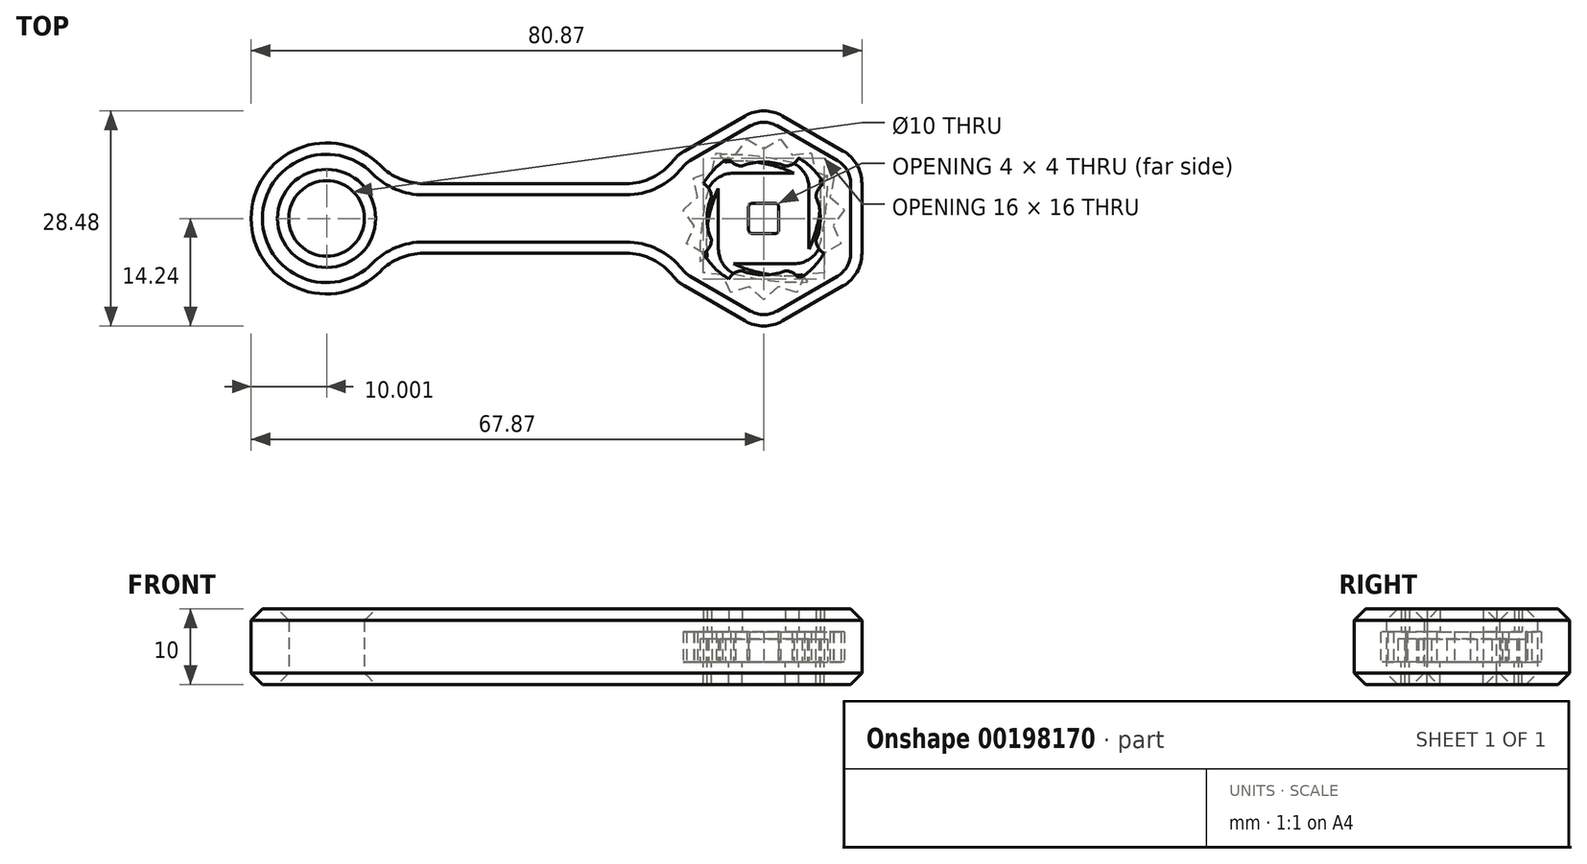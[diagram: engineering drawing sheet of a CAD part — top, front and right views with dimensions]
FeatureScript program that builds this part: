
annotation { "Feature Type Name" : "Feature", "Feature Type Description" : "" }
export const myFeature = defineFeature(function(context is Context, id is Id, definition is map)
    precondition{}
    {
        {
            var Q0;
            Q0=qCreatedBy(makeId("Top.planeOp"),FACE);
            var sketch = newSketch(context, id + "F0", { "sketchPlane" : qUnion([Q0])});
            skCircle(sketch, "E0.cCircle", {"center": v(0, 0) * mm, "radius": 13 * mm, "construction": true});
            skLineSegment(sketch, "E0.0", {"start": v(13, 4.62) * mm, "end": v(13, -4.62) * mm});
            skLineSegment(sketch, "E0.1", {"start": v(10.5, -8.95) * mm, "end": v(2.5, -13.57) * mm});
            skLineSegment(sketch, "E0.2", {"start": v(-2.5, -13.57) * mm, "end": v(-10.5, -8.95) * mm});
            skLineSegment(sketch, "E0.3", {"start": v(-13, -4.62) * mm, "end": v(-13, 4.62) * mm});
            skLineSegment(sketch, "E0.4", {"start": v(-10.5, 8.95) * mm, "end": v(-2.5, 13.57) * mm});
            skLineSegment(sketch, "E0.5", {"start": v(2.5, 13.57) * mm, "end": v(10.5, 8.95) * mm});
            skPoint(sketch, "E0.0.midPoint", {"position": v(13, 0) * mm});
            skPoint(sketch, "E1.visualSharp", {"position": v(0, 15.01) * mm});
            skArc(sketch, "E1.filletArc", {"start": v(2.5, 13.57) * mm, "mid": v(0, 14.24) * mm, "end": v(-2.5, 13.57) * mm});
            skPoint(sketch, "E2.visualSharp", {"position": v(13, 7.5) * mm});
            skArc(sketch, "E2.filletArc", {"start": v(13, 4.62) * mm, "mid": v(12.33, 7.12) * mm, "end": v(10.5, 8.95) * mm});
            skPoint(sketch, "E3.visualSharp", {"position": v(13, -7.5) * mm});
            skArc(sketch, "E3.filletArc", {"start": v(10.5, -8.95) * mm, "mid": v(12.33, -7.12) * mm, "end": v(13, -4.62) * mm});
            skPoint(sketch, "E4.visualSharp", {"position": v(0, -15.01) * mm});
            skArc(sketch, "E4.filletArc", {"start": v(-2.5, -13.57) * mm, "mid": v(0, -14.24) * mm, "end": v(2.5, -13.57) * mm});
            skPoint(sketch, "E5.visualSharp", {"position": v(-13, -7.5) * mm});
            skArc(sketch, "E5.filletArc", {"start": v(-13, -4.62) * mm, "mid": v(-12.33, -7.12) * mm, "end": v(-10.5, -8.95) * mm});
            skPoint(sketch, "E6.visualSharp", {"position": v(-13, 7.5) * mm});
            skArc(sketch, "E6.filletArc", {"start": v(-10.5, 8.95) * mm, "mid": v(-12.33, 7.12) * mm, "end": v(-13, 4.62) * mm});
            skCircle(sketch, "E7", {"center": v(0, 0) * mm, "radius": 9.24 * mm});
            skLineSegment(sketch, "E8", {"start": v(0, 9.24) * mm, "end": v(2.23, 10.5) * mm});
            skLineSegment(sketch, "E9", {"start": v(2.23, 10.5) * mm, "end": v(3.76, 8.44) * mm});
            skLineSegment(sketch, "E10.1.0", {"start": v(-3.76, 8.44) * mm, "end": v(-2.23, 10.5) * mm});
            skLineSegment(sketch, "E10.1.1", {"start": v(-2.23, 10.5) * mm, "end": v(0, 9.24) * mm});
            skLineSegment(sketch, "E10.2.0", {"start": v(-6.86, 6.18) * mm, "end": v(-6.31, 8.69) * mm});
            skLineSegment(sketch, "E10.2.1", {"start": v(-6.31, 8.69) * mm, "end": v(-3.76, 8.44) * mm});
            skLineSegment(sketch, "E10.3.0", {"start": v(-8.79, 2.85) * mm, "end": v(-9.3, 5.37) * mm});
            skLineSegment(sketch, "E10.3.1", {"start": v(-9.3, 5.37) * mm, "end": v(-6.86, 6.18) * mm});
            skLineSegment(sketch, "E10.4.0", {"start": v(-9.19, -0.97) * mm, "end": v(-10.68, 1.12) * mm});
            skLineSegment(sketch, "E10.4.1", {"start": v(-10.68, 1.12) * mm, "end": v(-8.79, 2.85) * mm});
            skLineSegment(sketch, "E10.5.0", {"start": v(-8, -4.62) * mm, "end": v(-10.21, -3.32) * mm});
            skLineSegment(sketch, "E10.5.1", {"start": v(-10.21, -3.32) * mm, "end": v(-9.19, -0.97) * mm});
            skLineSegment(sketch, "E10.6.0", {"start": v(-5.43, -7.47) * mm, "end": v(-7.98, -7.18) * mm});
            skLineSegment(sketch, "E10.6.1", {"start": v(-7.98, -7.18) * mm, "end": v(-8, -4.62) * mm});
            skLineSegment(sketch, "E10.7.0", {"start": v(-1.92, -9.04) * mm, "end": v(-4.37, -9.8) * mm});
            skLineSegment(sketch, "E10.7.1", {"start": v(-4.37, -9.8) * mm, "end": v(-5.43, -7.47) * mm});
            skLineSegment(sketch, "E10.8.0", {"start": v(1.92, -9.04) * mm, "end": v(0, -10.74) * mm});
            skLineSegment(sketch, "E10.8.1", {"start": v(0, -10.74) * mm, "end": v(-1.92, -9.04) * mm});
            skLineSegment(sketch, "E10.9.0", {"start": v(5.43, -7.47) * mm, "end": v(4.37, -9.8) * mm});
            skLineSegment(sketch, "E10.9.1", {"start": v(4.37, -9.8) * mm, "end": v(1.92, -9.04) * mm});
            skLineSegment(sketch, "E10.10.0", {"start": v(8, -4.62) * mm, "end": v(7.98, -7.18) * mm});
            skLineSegment(sketch, "E10.10.1", {"start": v(7.98, -7.18) * mm, "end": v(5.43, -7.47) * mm});
            skLineSegment(sketch, "E10.11.0", {"start": v(9.19, -0.97) * mm, "end": v(10.21, -3.32) * mm});
            skLineSegment(sketch, "E10.11.1", {"start": v(10.21, -3.32) * mm, "end": v(8, -4.62) * mm});
            skLineSegment(sketch, "E10.12.0", {"start": v(8.79, 2.85) * mm, "end": v(10.68, 1.12) * mm});
            skLineSegment(sketch, "E10.12.1", {"start": v(10.68, 1.12) * mm, "end": v(9.19, -0.97) * mm});
            skLineSegment(sketch, "E10.13.0", {"start": v(6.86, 6.18) * mm, "end": v(9.3, 5.37) * mm});
            skLineSegment(sketch, "E10.13.1", {"start": v(9.3, 5.37) * mm, "end": v(8.79, 2.85) * mm});
            skLineSegment(sketch, "E10.14.0", {"start": v(3.76, 8.44) * mm, "end": v(6.31, 8.69) * mm});
            skLineSegment(sketch, "E10.14.1", {"start": v(6.31, 8.69) * mm, "end": v(6.86, 6.18) * mm});
            skLineSegment(sketch, "E11.bottom", {"start": v(-13, 4.62) * mm, "end": v(-49, 4.62) * mm});
            skLineSegment(sketch, "E11.top", {"start": v(-13, -4.62) * mm, "end": v(-49, -4.62) * mm});
            skLineSegment(sketch, "E11.left", {"start": v(-13, 4.62) * mm, "end": v(-13, -4.62) * mm});
            skCircle(sketch, "E12", {"center": v(-57.87, 0) * mm, "radius": 5 * mm});
            skCircle(sketch, "E13", {"center": v(-57.87, 0) * mm, "radius": 10 * mm});
            skSolve(sketch);
        }
        {
            var Q0;
            Q0=makeQuery(id+"F0.imprint","IMPRINT",FACE,{"disambiguationData":[TD([[makeQuery(id+"F0.imprint","IMPRINT",EDGE,{"derivedFrom":sQuery(id+"F0.wireOp",EDGE,"E0.0")}),-1.0]])]});
            extrude(context, id + "F1", {"entities" : qUnion([Q0]), "endBound" : BoundingType.SYMMETRIC, "depth" : 4 * mm});
        }
        {
            var Q0;
            Q0=makeQuery(id+"F0.imprint","IMPRINT",FACE,{"disambiguationData":[TD([[makeQuery(id+"F0.imprint","IMPRINT",EDGE,{"derivedFrom":sQuery(id+"F0.wireOp",EDGE,"E12")}),-1.0]])]});
            var Q1;
            {var subQ0=sQuery(id+"F0.wireOp",EDGE,"E11.bottom");Q1=makeQuery(id+"F0.imprint","IMPRINT",FACE,{"disambiguationData":[TD([[makeQuery(id+"F0.imprint","IMPRINT",EDGE,{"derivedFrom":subQ0}),1.0]])]});}
            extrude(context, id + "F2", {"entities" : qUnion([Q0, Q1]), "operationType" : NewBodyOperationType.ADD, "endBound" : BoundingType.SYMMETRIC, "depth" : 10 * mm});
        }
        {
            var Q0;
            Q0=makeQuery(id+"F1.opExtrude","CAP_FACE",FACE,{"disambiguationData":[OSD([sQuery(id+"F0.wireOp",EDGE,"E0.0"),sQuery(id+"F0.wireOp",EDGE,"E0.1"),sQuery(id+"F0.wireOp",EDGE,"E0.2"),sQuery(id+"F0.wireOp",EDGE,"E0.4"),sQuery(id+"F0.wireOp",EDGE,"E0.5"),sQuery(id+"F0.wireOp",EDGE,"E1.filletArc"),sQuery(id+"F0.wireOp",EDGE,"E2.filletArc"),sQuery(id+"F0.wireOp",EDGE,"E3.filletArc"),sQuery(id+"F0.wireOp",EDGE,"E4.filletArc"),sQuery(id+"F0.wireOp",EDGE,"E5.filletArc"),sQuery(id+"F0.wireOp",EDGE,"E6.filletArc"),sQuery(id+"F0.wireOp",EDGE,"E8"),sQuery(id+"F0.wireOp",EDGE,"E9"),sQuery(id+"F0.wireOp",EDGE,"E10.1.0"),sQuery(id+"F0.wireOp",EDGE,"E10.1.1"),sQuery(id+"F0.wireOp",EDGE,"E10.2.0"),sQuery(id+"F0.wireOp",EDGE,"E10.2.1"),sQuery(id+"F0.wireOp",EDGE,"E10.3.0"),sQuery(id+"F0.wireOp",EDGE,"E10.3.1"),sQuery(id+"F0.wireOp",EDGE,"E10.4.0"),sQuery(id+"F0.wireOp",EDGE,"E10.4.1"),sQuery(id+"F0.wireOp",EDGE,"E10.5.0"),sQuery(id+"F0.wireOp",EDGE,"E10.5.1"),sQuery(id+"F0.wireOp",EDGE,"E10.6.0"),sQuery(id+"F0.wireOp",EDGE,"E10.6.1"),sQuery(id+"F0.wireOp",EDGE,"E10.7.0"),sQuery(id+"F0.wireOp",EDGE,"E10.7.1"),sQuery(id+"F0.wireOp",EDGE,"E10.8.0"),sQuery(id+"F0.wireOp",EDGE,"E10.8.1"),sQuery(id+"F0.wireOp",EDGE,"E10.9.0"),sQuery(id+"F0.wireOp",EDGE,"E10.9.1"),sQuery(id+"F0.wireOp",EDGE,"E10.10.0"),sQuery(id+"F0.wireOp",EDGE,"E10.10.1"),sQuery(id+"F0.wireOp",EDGE,"E10.11.0"),sQuery(id+"F0.wireOp",EDGE,"E10.11.1"),sQuery(id+"F0.wireOp",EDGE,"E10.12.0"),sQuery(id+"F0.wireOp",EDGE,"E10.12.1"),sQuery(id+"F0.wireOp",EDGE,"E10.13.0"),sQuery(id+"F0.wireOp",EDGE,"E10.13.1"),sQuery(id+"F0.wireOp",EDGE,"E10.14.0"),sQuery(id+"F0.wireOp",EDGE,"E10.14.1"),sQuery(id+"F0.wireOp",EDGE,"E10.15.0"),sQuery(id+"F0.wireOp",EDGE,"E10.15.1"),sQuery(id+"F0.wireOp",EDGE,"E10.16.0"),sQuery(id+"F0.wireOp",EDGE,"E10.16.1"),sQuery(id+"F0.wireOp",EDGE,"E10.17.0"),sQuery(id+"F0.wireOp",EDGE,"E10.17.1"),sQuery(id+"F0.wireOp",EDGE,"E10.18.0"),sQuery(id+"F0.wireOp",EDGE,"E10.18.1"),sQuery(id+"F0.wireOp",EDGE,"E10.19.0"),sQuery(id+"F0.wireOp",EDGE,"E10.19.1"),sQuery(id+"F0.wireOp",EDGE,"E11.left")])],"isStart":false});
            var sketch = newSketch(context, id + "F3", { "sketchPlane" : qUnion([Q0])});
            skArc(sketch, "E14", {"start": v(-4.62, 8) * mm, "mid": v(-6.53, 6.53) * mm, "end": v(-8, 4.62) * mm});
            skArc(sketch, "E15", {"start": v(2.85, 6.94) * mm, "mid": v(0, 7.5) * mm, "end": v(-2.85, 6.94) * mm});
            skArc(sketch, "E16", {"start": v(8, 4.62) * mm, "mid": v(7.22, 3.88) * mm, "end": v(6.94, 2.85) * mm});
            skArc(sketch, "E17", {"start": v(6.94, -2.85) * mm, "mid": v(7.22, -3.88) * mm, "end": v(8, -4.62) * mm});
            skArc(sketch, "E18.1.0", {"start": v(-4.62, 8) * mm, "mid": v(-3.88, 7.22) * mm, "end": v(-2.85, 6.94) * mm});
            skArc(sketch, "E18.1.1", {"start": v(2.85, 6.94) * mm, "mid": v(3.88, 7.22) * mm, "end": v(4.62, 8) * mm});
            skArc(sketch, "E18.2.0", {"start": v(-8, -4.62) * mm, "mid": v(-7.22, -3.88) * mm, "end": v(-6.94, -2.85) * mm});
            skArc(sketch, "E18.2.1", {"start": v(-6.94, 2.85) * mm, "mid": v(-7.22, 3.88) * mm, "end": v(-8, 4.62) * mm});
            skArc(sketch, "E18.3.0", {"start": v(4.62, -8) * mm, "mid": v(3.88, -7.22) * mm, "end": v(2.85, -6.94) * mm});
            skArc(sketch, "E18.3.1", {"start": v(-2.85, -6.94) * mm, "mid": v(-3.88, -7.22) * mm, "end": v(-4.62, -8) * mm});
            skArc(sketch, "E19.trimOffspring", {"start": v(6.94, -2.85) * mm, "mid": v(7.5, 0) * mm, "end": v(6.94, 2.85) * mm});
            skArc(sketch, "E20.trimOffspring", {"start": v(-2.85, -6.94) * mm, "mid": v(0, -7.5) * mm, "end": v(2.85, -6.94) * mm});
            skArc(sketch, "E21.trimOffspring", {"start": v(-6.94, 2.85) * mm, "mid": v(-7.5, 0) * mm, "end": v(-6.94, -2.85) * mm});
            skArc(sketch, "E22.trimOffspring", {"start": v(8, 4.62) * mm, "mid": v(6.53, 6.53) * mm, "end": v(4.62, 8) * mm});
            skArc(sketch, "E23.trimOffspring", {"start": v(4.62, -8) * mm, "mid": v(6.53, -6.53) * mm, "end": v(8, -4.62) * mm});
            skArc(sketch, "E24.trimOffspring", {"start": v(-8, -4.62) * mm, "mid": v(-6.53, -6.53) * mm, "end": v(-4.62, -8) * mm});
            skCircle(sketch, "E25.cCircle", {"center": v(0, 0) * mm, "radius": 13 * mm, "construction": true});
            skLineSegment(sketch, "E25.0", {"start": v(13, 4.62) * mm, "end": v(13, -4.62) * mm});
            skLineSegment(sketch, "E25.1", {"start": v(10.5, -8.95) * mm, "end": v(2.5, -13.57) * mm});
            skLineSegment(sketch, "E25.2", {"start": v(-2.5, -13.57) * mm, "end": v(-10.5, -8.95) * mm});
            skLineSegment(sketch, "E25.3", {"start": v(-13, -4.62) * mm, "end": v(-13, 4.62) * mm});
            skLineSegment(sketch, "E25.4", {"start": v(-10.5, 8.95) * mm, "end": v(-2.5, 13.57) * mm});
            skLineSegment(sketch, "E25.5", {"start": v(2.5, 13.57) * mm, "end": v(10.5, 8.95) * mm});
            skPoint(sketch, "E25.0.midPoint", {"position": v(13, 0) * mm});
            skPoint(sketch, "E26.visualSharp", {"position": v(13, 7.5) * mm});
            skArc(sketch, "E26.filletArc", {"start": v(13, 4.62) * mm, "mid": v(12.33, 7.12) * mm, "end": v(10.5, 8.95) * mm});
            skPoint(sketch, "E27.visualSharp", {"position": v(13, -7.5) * mm});
            skArc(sketch, "E27.filletArc", {"start": v(10.5, -8.95) * mm, "mid": v(12.33, -7.12) * mm, "end": v(13, -4.62) * mm});
            skPoint(sketch, "E28.visualSharp", {"position": v(0, -15.01) * mm});
            skArc(sketch, "E28.filletArc", {"start": v(-2.5, -13.57) * mm, "mid": v(0, -14.24) * mm, "end": v(2.5, -13.57) * mm});
            skPoint(sketch, "E29.visualSharp", {"position": v(-13, -7.5) * mm});
            skArc(sketch, "E29.filletArc", {"start": v(-13, -4.62) * mm, "mid": v(-12.33, -7.12) * mm, "end": v(-10.5, -8.95) * mm});
            skPoint(sketch, "E30.visualSharp", {"position": v(-13, 7.5) * mm});
            skArc(sketch, "E30.filletArc", {"start": v(-10.5, 8.95) * mm, "mid": v(-12.33, 7.12) * mm, "end": v(-13, 4.62) * mm});
            skPoint(sketch, "E31.visualSharp", {"position": v(0, 15.01) * mm});
            skArc(sketch, "E31.filletArc", {"start": v(2.5, 13.57) * mm, "mid": v(0, 14.24) * mm, "end": v(-2.5, 13.57) * mm});
            skSolve(sketch);
        }
        {
            var Q0;
            Q0 = qSketchRegion(id + "F3", true);
            extrude(context, id + "F4", {"entities" : qUnion([Q0]), "operationType" : NewBodyOperationType.ADD, "depth" : 3 * mm});
        }
        {
            var Q0;
            Q0=makeQuery(id+"F1.opExtrude","CAP_FACE",FACE,{"disambiguationData":[OSD([sQuery(id+"F0.wireOp",EDGE,"E0.0"),sQuery(id+"F0.wireOp",EDGE,"E0.1"),sQuery(id+"F0.wireOp",EDGE,"E0.2"),sQuery(id+"F0.wireOp",EDGE,"E0.4"),sQuery(id+"F0.wireOp",EDGE,"E0.5"),sQuery(id+"F0.wireOp",EDGE,"E1.filletArc"),sQuery(id+"F0.wireOp",EDGE,"E2.filletArc"),sQuery(id+"F0.wireOp",EDGE,"E3.filletArc"),sQuery(id+"F0.wireOp",EDGE,"E4.filletArc"),sQuery(id+"F0.wireOp",EDGE,"E5.filletArc"),sQuery(id+"F0.wireOp",EDGE,"E6.filletArc"),sQuery(id+"F0.wireOp",EDGE,"E8"),sQuery(id+"F0.wireOp",EDGE,"E9"),sQuery(id+"F0.wireOp",EDGE,"E10.1.0"),sQuery(id+"F0.wireOp",EDGE,"E10.1.1"),sQuery(id+"F0.wireOp",EDGE,"E10.2.0"),sQuery(id+"F0.wireOp",EDGE,"E10.2.1"),sQuery(id+"F0.wireOp",EDGE,"E10.3.0"),sQuery(id+"F0.wireOp",EDGE,"E10.3.1"),sQuery(id+"F0.wireOp",EDGE,"E10.4.0"),sQuery(id+"F0.wireOp",EDGE,"E10.4.1"),sQuery(id+"F0.wireOp",EDGE,"E10.5.0"),sQuery(id+"F0.wireOp",EDGE,"E10.5.1"),sQuery(id+"F0.wireOp",EDGE,"E10.6.0"),sQuery(id+"F0.wireOp",EDGE,"E10.6.1"),sQuery(id+"F0.wireOp",EDGE,"E10.7.0"),sQuery(id+"F0.wireOp",EDGE,"E10.7.1"),sQuery(id+"F0.wireOp",EDGE,"E10.8.0"),sQuery(id+"F0.wireOp",EDGE,"E10.8.1"),sQuery(id+"F0.wireOp",EDGE,"E10.9.0"),sQuery(id+"F0.wireOp",EDGE,"E10.9.1"),sQuery(id+"F0.wireOp",EDGE,"E10.10.0"),sQuery(id+"F0.wireOp",EDGE,"E10.10.1"),sQuery(id+"F0.wireOp",EDGE,"E10.11.0"),sQuery(id+"F0.wireOp",EDGE,"E10.11.1"),sQuery(id+"F0.wireOp",EDGE,"E10.12.0"),sQuery(id+"F0.wireOp",EDGE,"E10.12.1"),sQuery(id+"F0.wireOp",EDGE,"E10.13.0"),sQuery(id+"F0.wireOp",EDGE,"E10.13.1"),sQuery(id+"F0.wireOp",EDGE,"E10.14.0"),sQuery(id+"F0.wireOp",EDGE,"E10.14.1"),sQuery(id+"F0.wireOp",EDGE,"E10.15.0"),sQuery(id+"F0.wireOp",EDGE,"E10.15.1"),sQuery(id+"F0.wireOp",EDGE,"E10.16.0"),sQuery(id+"F0.wireOp",EDGE,"E10.16.1"),sQuery(id+"F0.wireOp",EDGE,"E10.17.0"),sQuery(id+"F0.wireOp",EDGE,"E10.17.1"),sQuery(id+"F0.wireOp",EDGE,"E10.18.0"),sQuery(id+"F0.wireOp",EDGE,"E10.18.1"),sQuery(id+"F0.wireOp",EDGE,"E10.19.0"),sQuery(id+"F0.wireOp",EDGE,"E10.19.1"),sQuery(id+"F0.wireOp",EDGE,"E11.left")])],"isStart":true});
            var sketch = newSketch(context, id + "F5", { "sketchPlane" : qUnion([Q0])});
            skArc(sketch, "E32", {"start": v(-4.62, 8) * mm, "mid": v(-6.53, 6.53) * mm, "end": v(-8, 4.62) * mm});
            skArc(sketch, "E33", {"start": v(2.85, 6.94) * mm, "mid": v(0, 7.5) * mm, "end": v(-2.85, 6.94) * mm});
            skArc(sketch, "E34", {"start": v(8, 4.62) * mm, "mid": v(7.22, 3.88) * mm, "end": v(6.94, 2.85) * mm});
            skArc(sketch, "E35", {"start": v(6.94, -2.85) * mm, "mid": v(7.22, -3.88) * mm, "end": v(8, -4.62) * mm});
            skArc(sketch, "E36.1.0", {"start": v(-4.62, 8) * mm, "mid": v(-3.88, 7.22) * mm, "end": v(-2.85, 6.94) * mm});
            skArc(sketch, "E36.1.1", {"start": v(2.85, 6.94) * mm, "mid": v(3.88, 7.22) * mm, "end": v(4.62, 8) * mm});
            skArc(sketch, "E36.2.0", {"start": v(-8, -4.62) * mm, "mid": v(-7.22, -3.88) * mm, "end": v(-6.94, -2.85) * mm});
            skArc(sketch, "E36.2.1", {"start": v(-6.94, 2.85) * mm, "mid": v(-7.22, 3.88) * mm, "end": v(-8, 4.62) * mm});
            skArc(sketch, "E36.3.0", {"start": v(4.62, -8) * mm, "mid": v(3.88, -7.22) * mm, "end": v(2.85, -6.94) * mm});
            skArc(sketch, "E36.3.1", {"start": v(-2.85, -6.94) * mm, "mid": v(-3.88, -7.22) * mm, "end": v(-4.62, -8) * mm});
            skArc(sketch, "E37.trimOffspring", {"start": v(6.94, -2.85) * mm, "mid": v(7.5, 0) * mm, "end": v(6.94, 2.85) * mm});
            skArc(sketch, "E38.trimOffspring", {"start": v(-2.85, -6.94) * mm, "mid": v(0, -7.5) * mm, "end": v(2.85, -6.94) * mm});
            skArc(sketch, "E39.trimOffspring", {"start": v(-6.94, 2.85) * mm, "mid": v(-7.5, 0) * mm, "end": v(-6.94, -2.85) * mm});
            skArc(sketch, "E40.trimOffspring", {"start": v(8, 4.62) * mm, "mid": v(6.53, 6.53) * mm, "end": v(4.62, 8) * mm});
            skArc(sketch, "E41.trimOffspring", {"start": v(4.62, -8) * mm, "mid": v(6.53, -6.53) * mm, "end": v(8, -4.62) * mm});
            skArc(sketch, "E42.trimOffspring", {"start": v(-8, -4.62) * mm, "mid": v(-6.53, -6.53) * mm, "end": v(-4.62, -8) * mm});
            skCircle(sketch, "E43.cCircle", {"center": v(0, 0) * mm, "radius": 13 * mm, "construction": true});
            skLineSegment(sketch, "E43.0", {"start": v(13, 4.62) * mm, "end": v(13, -4.62) * mm});
            skLineSegment(sketch, "E43.1", {"start": v(10.5, -8.95) * mm, "end": v(2.5, -13.57) * mm});
            skLineSegment(sketch, "E43.2", {"start": v(-2.5, -13.57) * mm, "end": v(-10.5, -8.95) * mm});
            skLineSegment(sketch, "E43.3", {"start": v(-13, -4.62) * mm, "end": v(-13, 4.62) * mm});
            skLineSegment(sketch, "E43.4", {"start": v(-10.5, 8.95) * mm, "end": v(-2.5, 13.57) * mm});
            skLineSegment(sketch, "E43.5", {"start": v(2.5, 13.57) * mm, "end": v(10.5, 8.95) * mm});
            skPoint(sketch, "E43.0.midPoint", {"position": v(13, 0) * mm});
            skPoint(sketch, "E44.visualSharp", {"position": v(13, 7.5) * mm});
            skArc(sketch, "E44.filletArc", {"start": v(13, 4.62) * mm, "mid": v(12.33, 7.12) * mm, "end": v(10.5, 8.95) * mm});
            skPoint(sketch, "E45.visualSharp", {"position": v(13, -7.5) * mm});
            skArc(sketch, "E45.filletArc", {"start": v(10.5, -8.95) * mm, "mid": v(12.33, -7.12) * mm, "end": v(13, -4.62) * mm});
            skPoint(sketch, "E46.visualSharp", {"position": v(0, -15.01) * mm});
            skArc(sketch, "E46.filletArc", {"start": v(-2.5, -13.57) * mm, "mid": v(0, -14.24) * mm, "end": v(2.5, -13.57) * mm});
            skPoint(sketch, "E47.visualSharp", {"position": v(-13, -7.5) * mm});
            skArc(sketch, "E47.filletArc", {"start": v(-13, -4.62) * mm, "mid": v(-12.33, -7.12) * mm, "end": v(-10.5, -8.95) * mm});
            skPoint(sketch, "E48.visualSharp", {"position": v(-13, 7.5) * mm});
            skArc(sketch, "E48.filletArc", {"start": v(-10.5, 8.95) * mm, "mid": v(-12.33, 7.12) * mm, "end": v(-13, 4.62) * mm});
            skPoint(sketch, "E49.visualSharp", {"position": v(0, 15.01) * mm});
            skArc(sketch, "E49.filletArc", {"start": v(2.5, 13.57) * mm, "mid": v(0, 14.24) * mm, "end": v(-2.5, 13.57) * mm});
            skSolve(sketch);
        }
        {
            var Q0;
            Q0 = qSketchRegion(id + "F5", true);
            extrude(context, id + "F6", {"entities" : qUnion([Q0]), "operationType" : NewBodyOperationType.ADD, "depth" : 3 * mm});
        }
        {
            var Q0;
            Q0=makeQuery(id+"F2.opExtrude","SWEPT_EDGE",EDGE,{"disambiguationData":[OSD([sQuery(id+"F0.wireOp",EDGE,"E11.bottom"),sQuery(id+"F0.wireOp",EDGE,"E13")])]});
            var Q1;
            {var subQ0=sQuery(id+"F0.wireOp",EDGE,"E11.bottom");var subQ2=sQuery(id+"F0.wireOp",EDGE,"E13");var subQ3=sQuery(id+"F0.wireOp",EDGE,"E12");var subQ4=sQuery(id+"F0.wireOp",EDGE,"E11.left");var subQ5=sQuery(id+"F0.wireOp",EDGE,"E11.top");var subQ6=sQuery(id+"F0.wireOp",EDGE,"E6.filletArc");var subQ59=makeQuery(id+"F2.opExtrude","SWEPT_EDGE",EDGE,{"disambiguationData":[OSD([subQ6,subQ0,subQ4])]});Q1=makeQuery(id+"F6.boolean.opBoolean","MERGE",EDGE,{"derivedFrom":[makeQuery(id+"F2.boolean.opBoolean","SPLIT",EDGE,{"disambiguationData":[TD([makeQuery(id+"F2.opExtrude","CAP_FACE",FACE,{"disambiguationData":[OSD([subQ0,subQ5,subQ4,subQ3,subQ2])],"isStart":true})])],"derivedFrom":subQ59}),makeQuery(id+"F4.boolean.opBoolean","MERGE",EDGE,{"derivedFrom":[makeQuery(id+"F2.boolean.opBoolean","MERGE",EDGE,{"derivedFrom":[makeQuery(id+"F1.opExtrude","SWEPT_EDGE",EDGE,{"disambiguationData":[OSD([subQ6,subQ0,subQ4])]}),subQ59]}),makeQuery(id+"F2.boolean.opBoolean","SPLIT",EDGE,{"disambiguationData":[TD([makeQuery(id+"F2.opExtrude","CAP_FACE",FACE,{"disambiguationData":[OSD([subQ0,subQ5,subQ4,subQ3,subQ2])],"isStart":false})])],"derivedFrom":subQ59}),makeQuery(id+"F4.opExtrude","SWEPT_EDGE",EDGE,{"disambiguationData":[OSD([sQuery(id+"F3.wireOp",EDGE,"E25.3"),sQuery(id+"F3.wireOp",EDGE,"E30.filletArc")])]})]}),makeQuery(id+"F6.opExtrude","SWEPT_EDGE",EDGE,{"disambiguationData":[OSD([sQuery(id+"F5.wireOp",EDGE,"E43.3"),sQuery(id+"F5.wireOp",EDGE,"E47.filletArc")])]})]});}
            var Q2;
            {var subQ0=sQuery(id+"F0.wireOp",EDGE,"E11.top");var subQ2=sQuery(id+"F0.wireOp",EDGE,"E13");var subQ3=sQuery(id+"F0.wireOp",EDGE,"E12");var subQ4=sQuery(id+"F0.wireOp",EDGE,"E11.left");var subQ5=sQuery(id+"F0.wireOp",EDGE,"E11.bottom");var subQ6=sQuery(id+"F0.wireOp",EDGE,"E5.filletArc");var subQ59=makeQuery(id+"F2.opExtrude","SWEPT_EDGE",EDGE,{"disambiguationData":[OSD([subQ6,subQ0,subQ4])]});Q2=makeQuery(id+"F6.boolean.opBoolean","MERGE",EDGE,{"derivedFrom":[makeQuery(id+"F2.boolean.opBoolean","SPLIT",EDGE,{"disambiguationData":[TD([makeQuery(id+"F2.opExtrude","CAP_FACE",FACE,{"disambiguationData":[OSD([subQ5,subQ0,subQ4,subQ3,subQ2])],"isStart":true})])],"derivedFrom":subQ59}),makeQuery(id+"F4.boolean.opBoolean","MERGE",EDGE,{"derivedFrom":[makeQuery(id+"F2.boolean.opBoolean","MERGE",EDGE,{"derivedFrom":[makeQuery(id+"F1.opExtrude","SWEPT_EDGE",EDGE,{"disambiguationData":[OSD([subQ6,subQ0,subQ4])]}),subQ59]}),makeQuery(id+"F2.boolean.opBoolean","SPLIT",EDGE,{"disambiguationData":[TD([makeQuery(id+"F2.opExtrude","CAP_FACE",FACE,{"disambiguationData":[OSD([subQ5,subQ0,subQ4,subQ3,subQ2])],"isStart":false})])],"derivedFrom":subQ59}),makeQuery(id+"F4.opExtrude","SWEPT_EDGE",EDGE,{"disambiguationData":[OSD([sQuery(id+"F3.wireOp",EDGE,"E25.3"),sQuery(id+"F3.wireOp",EDGE,"E29.filletArc")])]})]}),makeQuery(id+"F6.opExtrude","SWEPT_EDGE",EDGE,{"disambiguationData":[OSD([sQuery(id+"F5.wireOp",EDGE,"E43.3"),sQuery(id+"F5.wireOp",EDGE,"E48.filletArc")])]})]});}
            var Q3;
            Q3=makeQuery(id+"F2.opExtrude","SWEPT_EDGE",EDGE,{"disambiguationData":[OSD([sQuery(id+"F0.wireOp",EDGE,"E11.top"),sQuery(id+"F0.wireOp",EDGE,"E13")])]});
            fillet(context, id + "F7", {"entities" : qUnion([Q0, Q1, Q2, Q3]), "radius" : 8 * mm, "tangentPropagation" : true, "allowEdgeOverflow" : false});
        }
        {
            var Q0;
            Q0=makeQuery(id+"F2.opExtrude","CAP_EDGE",EDGE,{"disambiguationData":[OSD([sQuery(id+"F0.wireOp",EDGE,"E11.top")])],"isStart":false});
            var Q1;
            Q1=makeQuery(id+"F2.opExtrude","CAP_EDGE",EDGE,{"disambiguationData":[OSD([sQuery(id+"F0.wireOp",EDGE,"E11.bottom")])],"isStart":false});
            var Q2;
            Q2=makeQuery(id+"F2.opExtrude","CAP_EDGE",EDGE,{"disambiguationData":[OSD([sQuery(id+"F0.wireOp",EDGE,"E12")])],"isStart":false});
            var Q3;
            Q3=makeQuery(id+"F2.opExtrude","CAP_EDGE",EDGE,{"disambiguationData":[OSD([sQuery(id+"F0.wireOp",EDGE,"E11.top")])],"isStart":true});
            var Q4;
            Q4=makeQuery(id+"F2.opExtrude","CAP_EDGE",EDGE,{"disambiguationData":[OSD([sQuery(id+"F0.wireOp",EDGE,"E11.bottom")])],"isStart":true});
            var Q5;
            Q5=makeQuery(id+"F2.opExtrude","CAP_EDGE",EDGE,{"disambiguationData":[OSD([sQuery(id+"F0.wireOp",EDGE,"E12")])],"isStart":true});
            chamfer(context, id + "F8", {"entities" : qUnion([Q0, Q1, Q2, Q3, Q4, Q5]), "width" : 1.5 * mm, "tangentPropagation" : true});
        }
        {
            var Q0;
            {var subQ0=sQuery(id+"F5.wireOp",EDGE,"E40.trimOffspring");var subQ1=sQuery(id+"F5.wireOp",EDGE,"E32");var subQ2=sQuery(id+"F5.wireOp",EDGE,"E36.1.1");var subQ3=sQuery(id+"F5.wireOp",EDGE,"E36.1.0");var subQ4=sQuery(id+"F5.wireOp",EDGE,"E33");var subQ5=makeQuery(id+"F6.opExtrude","CAP_FACE",FACE,{"disambiguationData":[OSD([subQ1,subQ4,sQuery(id+"F5.wireOp",EDGE,"E34"),sQuery(id+"F5.wireOp",EDGE,"E35"),subQ3,subQ2,sQuery(id+"F5.wireOp",EDGE,"E36.2.0"),sQuery(id+"F5.wireOp",EDGE,"E36.2.1"),sQuery(id+"F5.wireOp",EDGE,"E36.3.0"),sQuery(id+"F5.wireOp",EDGE,"E36.3.1"),sQuery(id+"F5.wireOp",EDGE,"E37.trimOffspring"),sQuery(id+"F5.wireOp",EDGE,"E38.trimOffspring"),sQuery(id+"F5.wireOp",EDGE,"E39.trimOffspring"),subQ0,sQuery(id+"F5.wireOp",EDGE,"E41.trimOffspring"),sQuery(id+"F5.wireOp",EDGE,"E42.trimOffspring"),sQuery(id+"F5.wireOp",EDGE,"E43.0"),sQuery(id+"F5.wireOp",EDGE,"E43.1"),sQuery(id+"F5.wireOp",EDGE,"E43.2"),sQuery(id+"F5.wireOp",EDGE,"E43.3"),sQuery(id+"F5.wireOp",EDGE,"E43.4"),sQuery(id+"F5.wireOp",EDGE,"E43.5"),sQuery(id+"F5.wireOp",EDGE,"E44.filletArc"),sQuery(id+"F5.wireOp",EDGE,"E45.filletArc"),sQuery(id+"F5.wireOp",EDGE,"E46.filletArc"),sQuery(id+"F5.wireOp",EDGE,"E47.filletArc"),sQuery(id+"F5.wireOp",EDGE,"E48.filletArc"),sQuery(id+"F5.wireOp",EDGE,"E49.filletArc")])],"isStart":true});Q0=makeQuery(id+"F6.boolean.opBoolean","SPLIT",FACE,{"disambiguationData":[TD([makeQuery(id+"F1.opExtrude","SWEPT_FACE",FACE,{"disambiguationData":[OSD([sQuery(id+"F0.wireOp",EDGE,"E10.8.0")])]}),makeQuery(id+"F1.opExtrude","SWEPT_FACE",FACE,{"disambiguationData":[OSD([sQuery(id+"F0.wireOp",EDGE,"E10.9.0")])]}),makeQuery(id+"F1.opExtrude","SWEPT_FACE",FACE,{"disambiguationData":[OSD([sQuery(id+"F0.wireOp",EDGE,"E10.9.1")])]}),makeQuery(id+"F1.opExtrude","SWEPT_FACE",FACE,{"disambiguationData":[OSD([sQuery(id+"F0.wireOp",EDGE,"E10.10.0")])]}),makeQuery(id+"F1.opExtrude","SWEPT_FACE",FACE,{"disambiguationData":[OSD([sQuery(id+"F0.wireOp",EDGE,"E10.10.1")])]}),makeQuery(id+"F1.opExtrude","SWEPT_FACE",FACE,{"disambiguationData":[OSD([sQuery(id+"F0.wireOp",EDGE,"E10.11.0")])]}),makeQuery(id+"F1.opExtrude","SWEPT_FACE",FACE,{"disambiguationData":[OSD([sQuery(id+"F0.wireOp",EDGE,"E10.11.1")])]}),makeQuery(id+"F1.opExtrude","SWEPT_FACE",FACE,{"disambiguationData":[OSD([sQuery(id+"F0.wireOp",EDGE,"E10.12.0")])]}),makeQuery(id+"F1.opExtrude","SWEPT_FACE",FACE,{"disambiguationData":[OSD([sQuery(id+"F0.wireOp",EDGE,"E10.12.1")])]}),makeQuery(id+"F1.opExtrude","SWEPT_FACE",FACE,{"disambiguationData":[OSD([sQuery(id+"F0.wireOp",EDGE,"E10.13.1")])]}),makeQuery(id+"F6.opExtrude","SWEPT_FACE",FACE,{"disambiguationData":[OSD([subQ1])]}),subQ5,makeQuery(id+"F6.opExtrude","SWEPT_FACE",FACE,{"disambiguationData":[OSD([subQ4])]}),makeQuery(id+"F6.opExtrude","SWEPT_FACE",FACE,{"disambiguationData":[OSD([subQ3])]}),makeQuery(id+"F6.opExtrude","SWEPT_FACE",FACE,{"disambiguationData":[OSD([subQ2])]}),makeQuery(id+"F6.opExtrude","SWEPT_FACE",FACE,{"disambiguationData":[OSD([subQ0])]})])],"derivedFrom":subQ5});}
            var sketch = newSketch(context, id + "F9", { "sketchPlane" : qUnion([Q0])});
            skLineSegment(sketch, "E50.bottom", {"start": v(4, 6) * mm, "end": v(-4, 6) * mm});
            skLineSegment(sketch, "E50.top", {"start": v(4, -6) * mm, "end": v(-4, -6) * mm});
            skLineSegment(sketch, "E50.left", {"start": v(6, 4) * mm, "end": v(6, -4) * mm});
            skLineSegment(sketch, "E50.right", {"start": v(-6, 4) * mm, "end": v(-6, -4) * mm});
            skPoint(sketch, "E50.middle", {"position": v(0, 0) * mm});
            skPoint(sketch, "E51.visualSharp", {"position": v(-6, 6) * mm});
            skArc(sketch, "E51.filletArc", {"start": v(-4, 6) * mm, "mid": v(-5.41, 5.41) * mm, "end": v(-6, 4) * mm});
            skPoint(sketch, "E52.visualSharp", {"position": v(6, 6) * mm});
            skArc(sketch, "E52.filletArc", {"start": v(6, 4) * mm, "mid": v(5.41, 5.41) * mm, "end": v(4, 6) * mm});
            skPoint(sketch, "E53.visualSharp", {"position": v(6, -6) * mm});
            skArc(sketch, "E53.filletArc", {"start": v(4, -6) * mm, "mid": v(5.41, -5.41) * mm, "end": v(6, -4) * mm});
            skPoint(sketch, "E54.visualSharp", {"position": v(-6, -6) * mm});
            skArc(sketch, "E54.filletArc", {"start": v(-6, -4) * mm, "mid": v(-5.41, -5.41) * mm, "end": v(-4, -6) * mm});
            skArc(sketch, "E55", {"start": v(6, 4) * mm, "mid": v(5.46, 5.93) * mm, "end": v(4, 7.3) * mm});
            skLineSegment(sketch, "E56", {"start": v(-5.09, 7.47) * mm, "end": v(-5.76, 8.44) * mm});
            skArc(sketch, "E57", {"start": v(4, 7.3) * mm, "mid": v(-0.84, 8.2) * mm, "end": v(-5.76, 8.44) * mm});
            skArc(sketch, "E58", {"start": v(4, 6) * mm, "mid": v(-0.44, 7.37) * mm, "end": v(-5.09, 7.47) * mm});
            skArc(sketch, "E59.1.0", {"start": v(-7.3, 4) * mm, "mid": v(-8.2, -0.84) * mm, "end": v(-8.44, -5.76) * mm});
            skLineSegment(sketch, "E59.1.1", {"start": v(-7.47, -5.09) * mm, "end": v(-8.44, -5.76) * mm});
            skArc(sketch, "E59.1.2", {"start": v(-6, 4) * mm, "mid": v(-7.37, -0.44) * mm, "end": v(-7.47, -5.09) * mm});
            skArc(sketch, "E59.1.3", {"start": v(-4, 6) * mm, "mid": v(-5.93, 5.46) * mm, "end": v(-7.3, 4) * mm});
            skArc(sketch, "E59.2.0", {"start": v(-4, -7.3) * mm, "mid": v(0.84, -8.2) * mm, "end": v(5.76, -8.44) * mm});
            skLineSegment(sketch, "E59.2.1", {"start": v(5.09, -7.47) * mm, "end": v(5.76, -8.44) * mm});
            skArc(sketch, "E59.2.2", {"start": v(-4, -6) * mm, "mid": v(0.44, -7.37) * mm, "end": v(5.09, -7.47) * mm});
            skArc(sketch, "E59.2.3", {"start": v(-6, -4) * mm, "mid": v(-5.46, -5.93) * mm, "end": v(-4, -7.3) * mm});
            skArc(sketch, "E59.3.0", {"start": v(7.3, -4) * mm, "mid": v(8.2, 0.84) * mm, "end": v(8.44, 5.76) * mm});
            skLineSegment(sketch, "E59.3.1", {"start": v(7.47, 5.09) * mm, "end": v(8.44, 5.76) * mm});
            skArc(sketch, "E59.3.2", {"start": v(6, -4) * mm, "mid": v(7.37, 0.44) * mm, "end": v(7.47, 5.09) * mm});
            skArc(sketch, "E59.3.3", {"start": v(4, -6) * mm, "mid": v(5.93, -5.46) * mm, "end": v(7.3, -4) * mm});
            skLineSegment(sketch, "E60.bottom", {"start": v(1.5, 2) * mm, "end": v(-1.5, 2) * mm});
            skLineSegment(sketch, "E60.top", {"start": v(1.5, -2) * mm, "end": v(-1.5, -2) * mm});
            skLineSegment(sketch, "E60.left", {"start": v(2, 1.5) * mm, "end": v(2, -1.5) * mm});
            skLineSegment(sketch, "E60.right", {"start": v(-2, 1.5) * mm, "end": v(-2, -1.5) * mm});
            skPoint(sketch, "E61.visualSharp", {"position": v(-2, 2) * mm});
            skArc(sketch, "E61.filletArc", {"start": v(-1.5, 2) * mm, "mid": v(-1.85, 1.85) * mm, "end": v(-2, 1.5) * mm});
            skPoint(sketch, "E62.visualSharp", {"position": v(2, 2) * mm});
            skArc(sketch, "E62.filletArc", {"start": v(2, 1.5) * mm, "mid": v(1.85, 1.85) * mm, "end": v(1.5, 2) * mm});
            skPoint(sketch, "E63.visualSharp", {"position": v(2, -2) * mm});
            skArc(sketch, "E63.filletArc", {"start": v(1.5, -2) * mm, "mid": v(1.85, -1.85) * mm, "end": v(2, -1.5) * mm});
            skPoint(sketch, "E64.visualSharp", {"position": v(-2, -2) * mm});
            skArc(sketch, "E64.filletArc", {"start": v(-2, -1.5) * mm, "mid": v(-1.85, -1.85) * mm, "end": v(-1.5, -2) * mm});
            skSolve(sketch);
        }
        {
            var Q0;
            Q0 = qSketchRegion(id + "F9", true);
            extrude(context, id + "F10", {"entities" : qUnion([Q0]), "depth" : 3 * mm});
        }
    });
